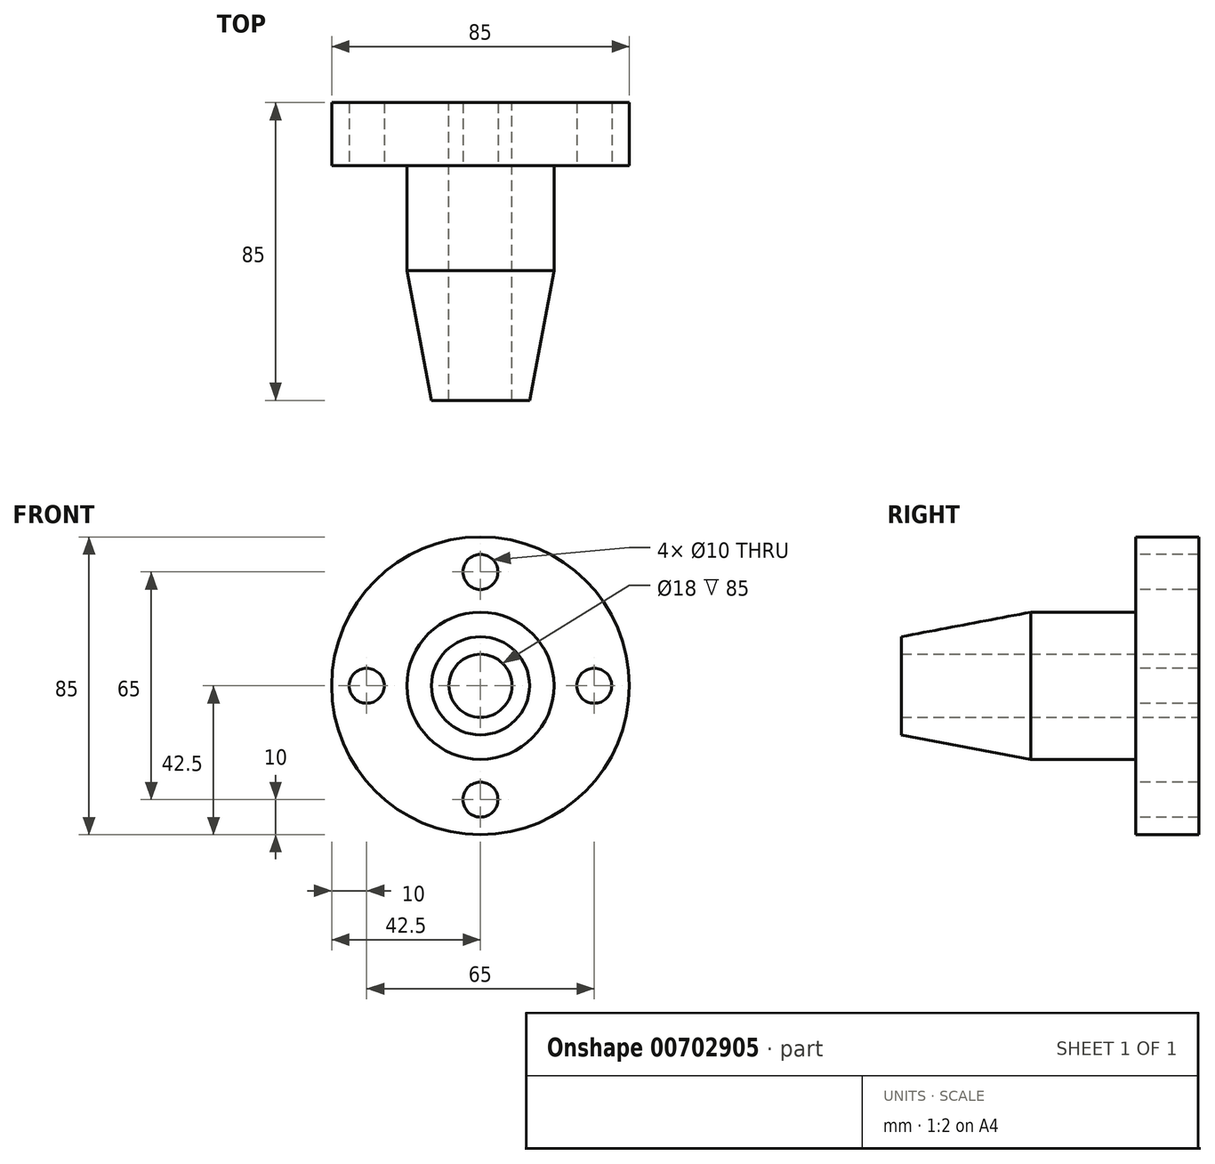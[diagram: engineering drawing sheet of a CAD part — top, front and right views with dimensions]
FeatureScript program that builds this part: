
annotation { "Feature Type Name" : "Feature", "Feature Type Description" : "" }
export const myFeature = defineFeature(function(context is Context, id is Id, definition is map)
    precondition{}
    {
        {
            var Q0;
            Q0=qCreatedBy(makeId("Top.planeOp"),FACE);
            var sketch = newSketch(context, id + "F0", { "sketchPlane" : qUnion([Q0])});
            skLineSegment(sketch, "E0", {"start": v(9, -42.5) * mm, "end": v(9, 42.5) * mm});
            skLineSegment(sketch, "E1", {"start": v(9, 42.5) * mm, "end": v(42.5, 42.5) * mm});
            skLineSegment(sketch, "E2", {"start": v(42.5, 42.5) * mm, "end": v(42.5, 24.5) * mm});
            skLineSegment(sketch, "E3", {"start": v(42.5, 24.5) * mm, "end": v(21, 24.5) * mm});
            skLineSegment(sketch, "E4", {"start": v(21, 24.5) * mm, "end": v(21, -5.5) * mm});
            skLineSegment(sketch, "E5", {"start": v(21, -5.5) * mm, "end": v(14, -42.5) * mm});
            skLineSegment(sketch, "E6", {"start": v(14, -42.5) * mm, "end": v(9, -42.5) * mm});
            skLineSegment(sketch, "E7", {"start": v(0, 55.5) * mm, "end": v(0, -59.5) * mm, "construction": true});
            skSolve(sketch);
        }
        {
            var Q0;
            Q0=makeQuery(id+"F0.imprint","IMPRINT",FACE,{"disambiguationData":[TD([[makeQuery(id+"F0.imprint","IMPRINT",EDGE,{"derivedFrom":sQuery(id+"F0.wireOp",EDGE,"E0")}),-1.0]])]});
            var Q1;
            Q1=sQuery(id+"F0.wireOp",EDGE,"E7");
            revolve(context, id + "F1", {"surfaceOperationType" : NewSurfaceOperationType.NEW, "entities" : qUnion([Q0]), "axis" : qUnion([Q1]), "revolveType" : RevolveType.FULL});
        }
        {
            var Q0;
            Q0=makeQuery(id+"F1.opRevolve","SWEPT_FACE",FACE,{"disambiguationData":[OSD([sQuery(id+"F0.wireOp",EDGE,"E3")])]});
            var sketch = newSketch(context, id + "F2", { "sketchPlane" : qUnion([Q0])});
            skPoint(sketch, "E8", {"position": v(0, 32.5) * mm});
            skPoint(sketch, "E9", {"position": v(-32.5, 0) * mm});
            skPoint(sketch, "E10", {"position": v(0, -32.5) * mm});
            skPoint(sketch, "E11", {"position": v(32.5, 0) * mm});
            skSolve(sketch);
        }
        {
            var Q0;
            Q0=sQuery(id+"F2.wireOp",VERTEX,"E8");
            var Q1;
            Q1=sQuery(id+"F2.wireOp",VERTEX,"E11");
            var Q2;
            Q2=sQuery(id+"F2.wireOp",VERTEX,"E10");
            var Q3;
            Q3=sQuery(id+"F2.wireOp",VERTEX,"E9");
            var Q4;
            Q4=makeQuery(id+"F1.opRevolve","SWEPT_BODY",BODY,{"disambiguationData":[OSD([sQuery(id+"F0.wireOp",EDGE,"E0"),sQuery(id+"F0.wireOp",EDGE,"E1"),sQuery(id+"F0.wireOp",EDGE,"E2"),sQuery(id+"F0.wireOp",EDGE,"E3"),sQuery(id+"F0.wireOp",EDGE,"E4"),sQuery(id+"F0.wireOp",EDGE,"E5"),sQuery(id+"F0.wireOp",EDGE,"E6")])]});
            hole(context, id + "F3", {"style" : HoleStyle.SIMPLE, "endStyle" : HoleEndStyle.THROUGH, "holeDiameter" : 10 * mm, "majorDiameter" : 5 * mm, "isTappedThrough" : true, "tappedDepth" : 12 * mm, "tapClearance" : 3, "locations" : qUnion([Q0, Q1, Q2, Q3]), "scope" : qUnion([Q4])});
        }
    });
